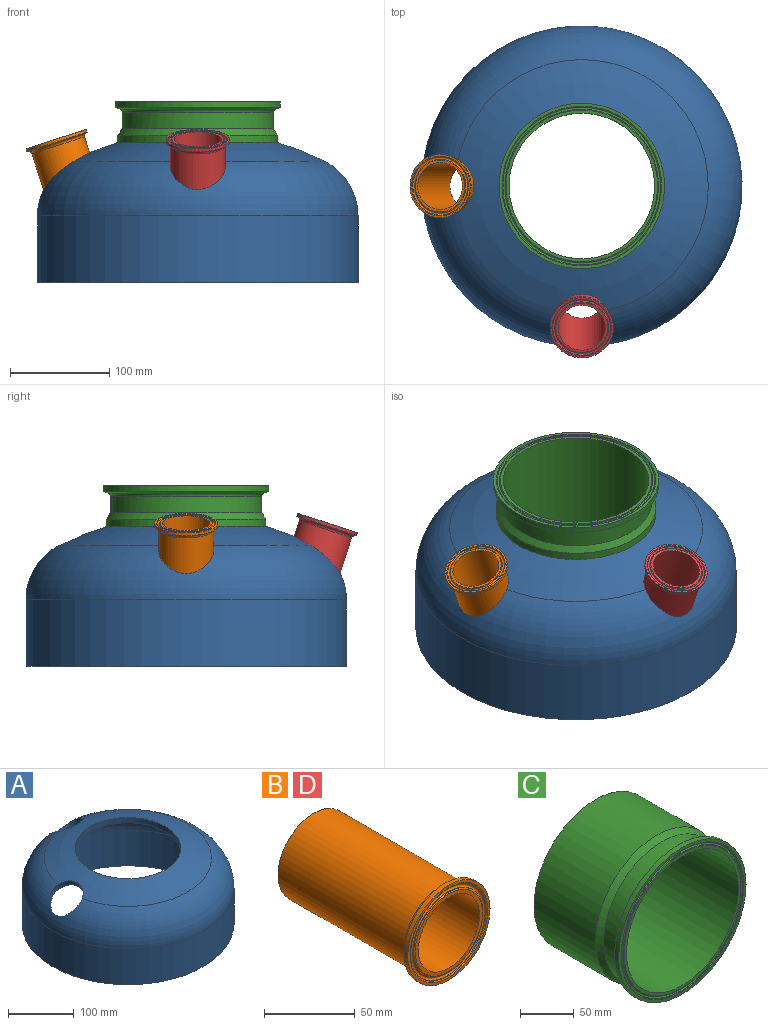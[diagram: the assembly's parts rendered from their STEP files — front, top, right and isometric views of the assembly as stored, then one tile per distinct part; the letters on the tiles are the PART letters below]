
ASSEMBLY  parts=4 mates=3
PART A: 10 faces, bbox 350x350x140.7 mm
  f0: cylinder r=27.84mm len=64.12mm, axis (0.31,0,-0.95), area 1923.8mm2, adj f1,f2,f3,f7
  f1: sphere r=274.32mm, area 28279.5mm2, adj f0,f3,f8,f9
  f2: sphere r=283.59mm, area 31635.8mm2, adj f0,f7,f8,f9
  f3: torus R=99.67mm, axis (0,0,-1), area 47872.6mm2, adj f0,f1,f4,f9
  f4: cylinder r=152.4mm len=304.8mm, axis (0,0,-1), area 63886.2mm2, adj f3,f5
  f5: plane 323.34x323.34mm, normal (0,0,-1), area 9147.5mm2, adj f4,f6
  f6: cylinder r=161.67mm len=323.34mm, axis (0,0,-1), area 67772.6mm2, adj f5,f7
  f7: torus R=99.67mm, axis (0,0,-1), area 60653.8mm2, adj f0,f2,f6,f9
  f8: cylinder r=80.64mm len=161.29mm, axis (0,0,-1), area 4907.3mm2, adj f1,f2
  f9: cylinder r=27.84mm len=64.13mm, axis (0,-0.31,-0.95), area 1924mm2, adj f1,f2,f3,f7
PART B: 13 faces, bbox 67.1x105x67.1 mm
  f0: cylinder r=31.95mm len=63.91mm, axis (0,-1,0), area 571.1mm2, adj f1,f10
  f1: cone r=29.93mm half-angle=70deg, axis (0,-1,0), area 419.1mm2, adj f0,f2
  f2: torus R=31.01mm, axis (0,-1,0), area 696.4mm2, adj f1,f3
  f3: cylinder r=27.84mm len=98.44mm, axis (0,-1,0), area 17218.2mm2, adj f2,f12
  f4: cylinder r=23.75mm len=105mm, axis (0,-1,0), area 15668.6mm2, adj f11,f12
  f5: torus R=26.18mm, axis (0,-1,0), area 153.8mm2, adj f6,f11
  f6: cone r=27.07mm half-angle=23deg, axis (0,1,0), area 72.4mm2, adj f5,f7
  f7: torus R=28.17mm, axis (0,-1,0), area 494.2mm2, adj f6,f8
  f8: cone r=29.43mm half-angle=23deg, axis (0,-1,0), area 78.8mm2, adj f7,f9
  f9: torus R=30.16mm, axis (0,-1,0), area 172.1mm2, adj f8,f10
  f10: plane 63.91x63.91mm, normal (0,-1,0), area 350.1mm2, adj f0,f9
  f11: plane 52.36x52.36mm, normal (0,-1,0), area 381mm2, adj f4,f5
  f12: plane 55.68x55.68mm, normal (0,1,0), area 662.8mm2, adj f3,f4
PART C: 15 faces, bbox 174.1x114.3x174.1 mm
  f0: cylinder r=76.2mm len=152.4mm, axis (0,-1,0), area 8023.1mm2, adj f9,f14
  f1: plane 166.88x166.88mm, normal (0,-1,0), area 1551.2mm2, adj f2,f11
  f2: torus R=80.43mm, axis (0,-1,0), area 462.9mm2, adj f1,f3
  f3: cone r=79.7mm half-angle=23deg, axis (0,-1,0), area 213.6mm2, adj f2,f4
  f4: torus R=78.44mm, axis (0,-1,0), area 1376mm2, adj f3,f5
  f5: cone r=77.34mm half-angle=23deg, axis (0,1,0), area 207.3mm2, adj f4,f6
  f6: torus R=76.44mm, axis (0,-1,0), area 444.6mm2, adj f5,f7
  f7: plane 152.89x152.89mm, normal (0,-1,0), area 1418.8mm2, adj f6,f8
  f8: cylinder r=73.43mm len=146.86mm, axis (0,-1,0), area 52736.1mm2, adj f7,f13
  f9: torus R=79.38mm, axis (0,-1,0), area 1875mm2, adj f0,f10
  f10: cone r=78.29mm half-angle=70deg, axis (0,-1,0), area 2784.5mm2, adj f9,f11
  f11: cylinder r=83.44mm len=166.88mm, axis (0,-1,0), area 2929.6mm2, adj f1,f10
  f12: cylinder r=80.54mm len=161.09mm, axis (0,-1,0), area 40863.4mm2, adj f13,f14
  f13: plane 161.09x161.09mm, normal (0,1,0), area 3440.3mm2, adj f8,f12
  f14: cone r=80.54mm half-angle=34.4deg, axis (0,1,0), area 3788.4mm2, adj f0,f12
PART D: same geometry as B
PLACE A rot(axis=(0,0,1),90deg) t=(0,0,0)mm
PLACE B rot(axis=(-0.63,-0.63,0.46),130.9deg) t=(-142.88,0,144.17)mm
PLACE C rot(axis=(-0.58,-0.58,0.58),120deg) t=(0,0,181.81)mm
PLACE D rot(axis=(-0.51,-0.7,0.51),110.2deg) t=(0,-142.88,144.17)mm
MATE fastened A.f8 <-> C.f12  axis (0,0,-1) through (0,0,131.01)mm
MATE fastened A.f0 <-> D.f0  axis (0,0.31,-0.95) through (0,-130.06,104.7)mm
MATE fastened A.f9 <-> B.f0  axis (0.31,0,-0.95) through (-130.06,0,104.7)mm
